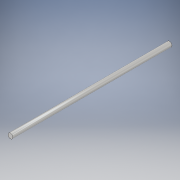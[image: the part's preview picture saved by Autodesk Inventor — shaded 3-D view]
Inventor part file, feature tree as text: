
AUTODESK INVENTOR PART (.ipt)
format: ipt  version: 2019 (Build 230136000, 136)  size: 92,160 bytes
history: native  units: in
note: dims shown in document units (in); Inventor stores cm internally (conversion verified against a paired STEP export)
features: extrude x1, sketch x1
ambient origin geometry x8: Origin, YZ Plane, XZ Plane, XY Plane, X Axis, Y Axis, Z Axis, Center Point
bodies: Solid1 (feature_tree)
feature tree (2):
  extrude  "Extrusion1"  Depth=12.0in TaperAngle=0.0deg
  sketch  "Sketch1"  dims[d0=0.375in d1=12.0in d2=0.0in]
